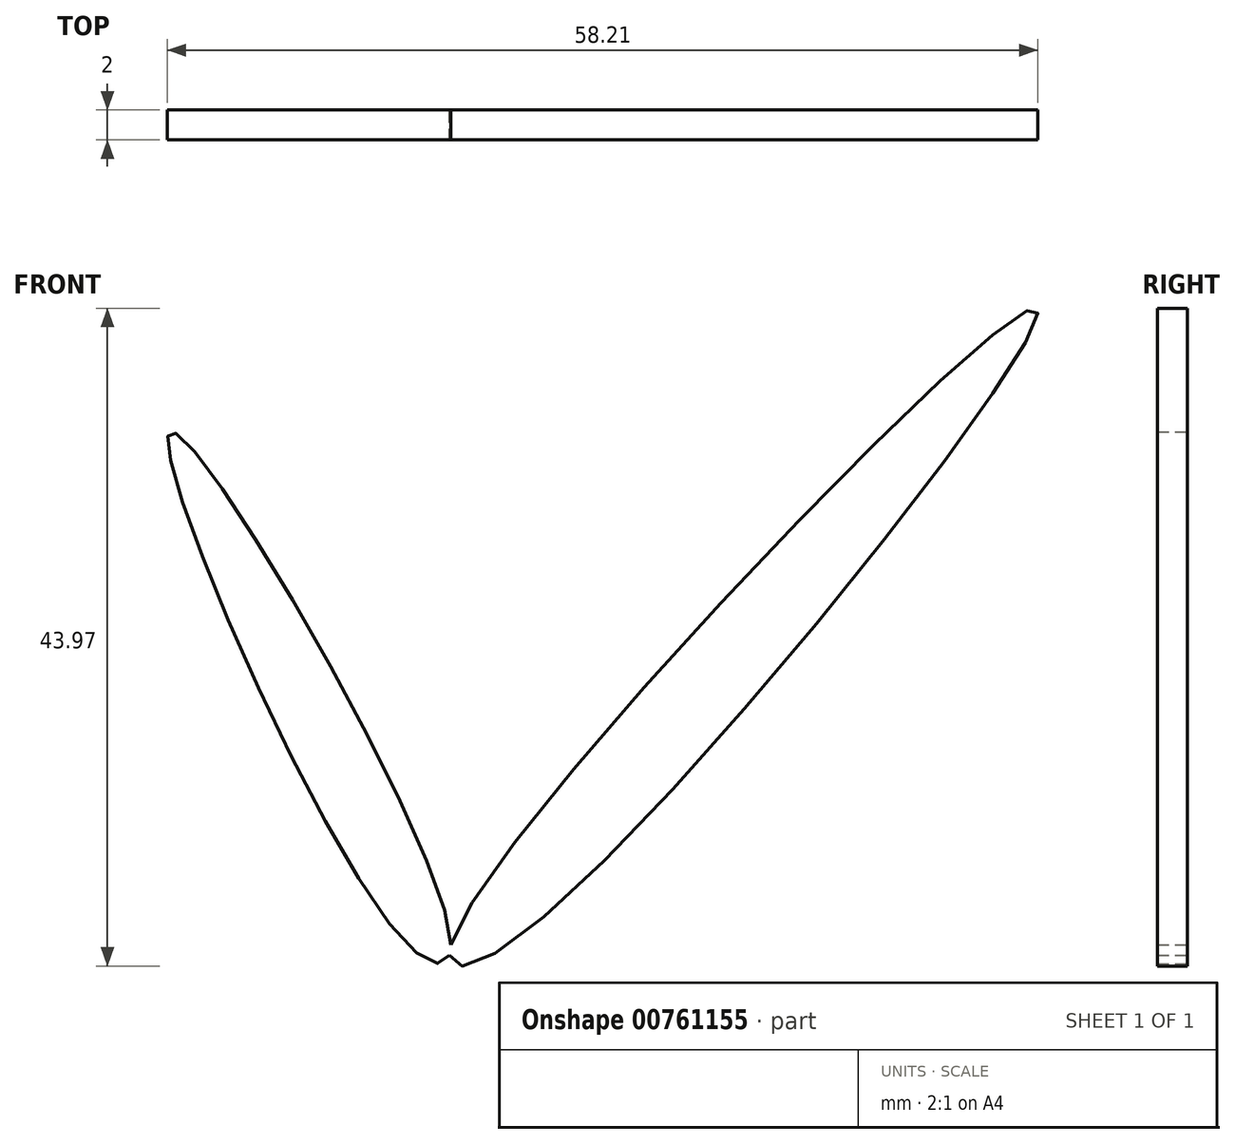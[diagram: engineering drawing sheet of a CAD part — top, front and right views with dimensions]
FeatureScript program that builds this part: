
annotation { "Feature Type Name" : "Feature", "Feature Type Description" : "" }
export const myFeature = defineFeature(function(context is Context, id is Id, definition is map)
    precondition{}
    {
        {
            var Q0;
            Q0=qCreatedBy(makeId("Front.planeOp"),FACE);
            var sketch = newSketch(context, id + "F0", { "sketchPlane" : qUnion([Q0])});
            skFitSpline(sketch, "E0", {"points": [v(0, 0) * mm, v(39.06, 42.56) * mm, v(3.8, 0) * mm, v(0, 0) * mm]});
            skFitSpline(sketch, "E1", {"points": [v(0, 0) * mm, v(-18.71, 34.3) * mm, v(-2.88, 0) * mm, v(0, 0) * mm]});
            skSolve(sketch);
        }
        {
            var Q0;
            Q0 = qSketchRegion(id + "F0", true);
            extrude(context, id + "F1", {"entities" : qUnion([Q0]), "depth" : 2 * mm, "offsetDistance" : 25.4 * mm});
        }
    });
